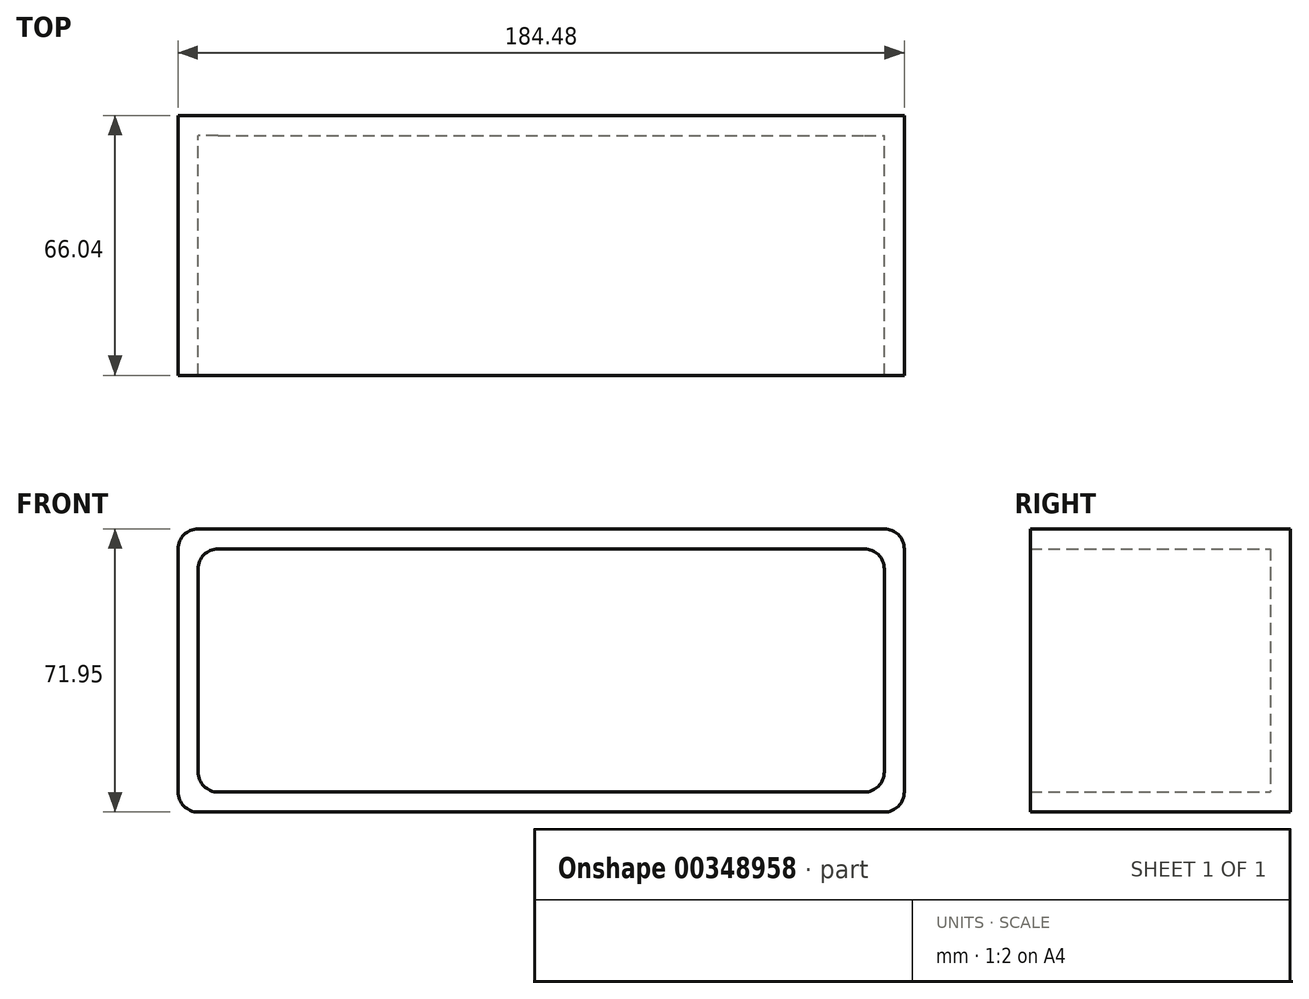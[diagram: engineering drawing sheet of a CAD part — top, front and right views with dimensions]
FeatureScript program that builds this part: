
annotation { "Feature Type Name" : "Feature", "Feature Type Description" : "" }
export const myFeature = defineFeature(function(context is Context, id is Id, definition is map)
    precondition{}
    {
        {
            var Q0;
            Q0=qCreatedBy(makeId("Front.planeOp"),FACE);
            var sketch = newSketch(context, id + "F0", { "sketchPlane" : qUnion([Q0])});
            skLineSegment(sketch, "E0.bottom", {"start": v(-90.66, 41.44) * mm, "end": v(93.82, 41.44) * mm});
            skLineSegment(sketch, "E0.top", {"start": v(-90.66, -30.5) * mm, "end": v(93.82, -30.5) * mm});
            skLineSegment(sketch, "E0.left", {"start": v(-90.66, 41.44) * mm, "end": v(-90.66, -30.5) * mm});
            skLineSegment(sketch, "E0.right", {"start": v(93.82, 41.44) * mm, "end": v(93.82, -30.5) * mm});
            skSolve(sketch);
        }
        {
            var Q0;
            Q0=makeQuery(id+"F0.imprint","IMPRINT",FACE,{"disambiguationData":[TD([[makeQuery(id+"F0.imprint","IMPRINT",EDGE,{"derivedFrom":sQuery(id+"F0.wireOp",EDGE,"E0.bottom")}),-1.0]])]});
            extrude(context, id + "F1", {"entities" : qUnion([Q0]), "depth" : 66.04 * mm});
        }
        {
            var Q0;
            Q0=makeQuery(id+"F1.opExtrude","CAP_FACE",FACE,{"disambiguationData":[OSD([sQuery(id+"F0.wireOp",EDGE,"E0.bottom"),sQuery(id+"F0.wireOp",EDGE,"E0.top"),sQuery(id+"F0.wireOp",EDGE,"E0.left"),sQuery(id+"F0.wireOp",EDGE,"E0.right")])],"isStart":false});
            shell(context, id + "F2", {"entities" : qUnion([Q0]), "thickness" : 5.08 * mm});
        }
        {
            var Q0;
            Q0=makeQuery(id+"F2.opShell","OFFSET_FACE",FACE,{"disambiguationData":[OSD([sQuery(id+"F0.wireOp",EDGE,"E0.bottom"),sQuery(id+"F0.wireOp",EDGE,"E0.top"),sQuery(id+"F0.wireOp",EDGE,"E0.left"),sQuery(id+"F0.wireOp",EDGE,"E0.right")])]});
            extrude(context, id + "F3", {"entities" : qUnion([Q0]), "operationType" : NewBodyOperationType.REMOVE, "oppositeDirection" : true, "depth" : -33.02 * mm});
        }
        {
            var Q0;
            Q0=makeQuery(id+"F1.opExtrude","SWEPT_EDGE",EDGE,{"disambiguationData":[OSD([sQuery(id+"F0.wireOp",EDGE,"E0.bottom"),sQuery(id+"F0.wireOp",EDGE,"E0.left")])]});
            var Q1;
            Q1=makeQuery(id+"F1.opExtrude","SWEPT_EDGE",EDGE,{"disambiguationData":[OSD([sQuery(id+"F0.wireOp",EDGE,"E0.bottom"),sQuery(id+"F0.wireOp",EDGE,"E0.right")])]});
            var Q2;
            Q2=makeQuery(id+"F1.opExtrude","SWEPT_EDGE",EDGE,{"disambiguationData":[OSD([sQuery(id+"F0.wireOp",EDGE,"E0.top"),sQuery(id+"F0.wireOp",EDGE,"E0.right")])]});
            var Q3;
            Q3=makeQuery(id+"F1.opExtrude","SWEPT_EDGE",EDGE,{"disambiguationData":[OSD([sQuery(id+"F0.wireOp",EDGE,"E0.top"),sQuery(id+"F0.wireOp",EDGE,"E0.left")])]});
            fillet(context, id + "F4", {"entities" : qUnion([Q0, Q1, Q2, Q3]), "radius" : 5.08 * mm, "tangentPropagation" : true, "allowEdgeOverflow" : false});
        }
        {
            var Q0;
            Q0=makeQuery(id+"F2.opShell","OFFSET_EDGE",EDGE,{"disambiguationData":[OSD([sQuery(id+"F0.wireOp",EDGE,"E0.top"),sQuery(id+"F0.wireOp",EDGE,"E0.left")])]});
            var Q1;
            Q1=makeQuery(id+"F2.opShell","OFFSET_EDGE",EDGE,{"disambiguationData":[OSD([sQuery(id+"F0.wireOp",EDGE,"E0.top"),sQuery(id+"F0.wireOp",EDGE,"E0.right")])]});
            var Q2;
            Q2=makeQuery(id+"F2.opShell","OFFSET_EDGE",EDGE,{"disambiguationData":[OSD([sQuery(id+"F0.wireOp",EDGE,"E0.bottom"),sQuery(id+"F0.wireOp",EDGE,"E0.right")])]});
            var Q3;
            Q3=makeQuery(id+"F2.opShell","OFFSET_EDGE",EDGE,{"disambiguationData":[OSD([sQuery(id+"F0.wireOp",EDGE,"E0.bottom"),sQuery(id+"F0.wireOp",EDGE,"E0.left")])]});
            fillet(context, id + "F5", {"entities" : qUnion([Q0, Q1, Q2, Q3]), "radius" : 5.08 * mm, "tangentPropagation" : true, "allowEdgeOverflow" : false});
        }
    });
